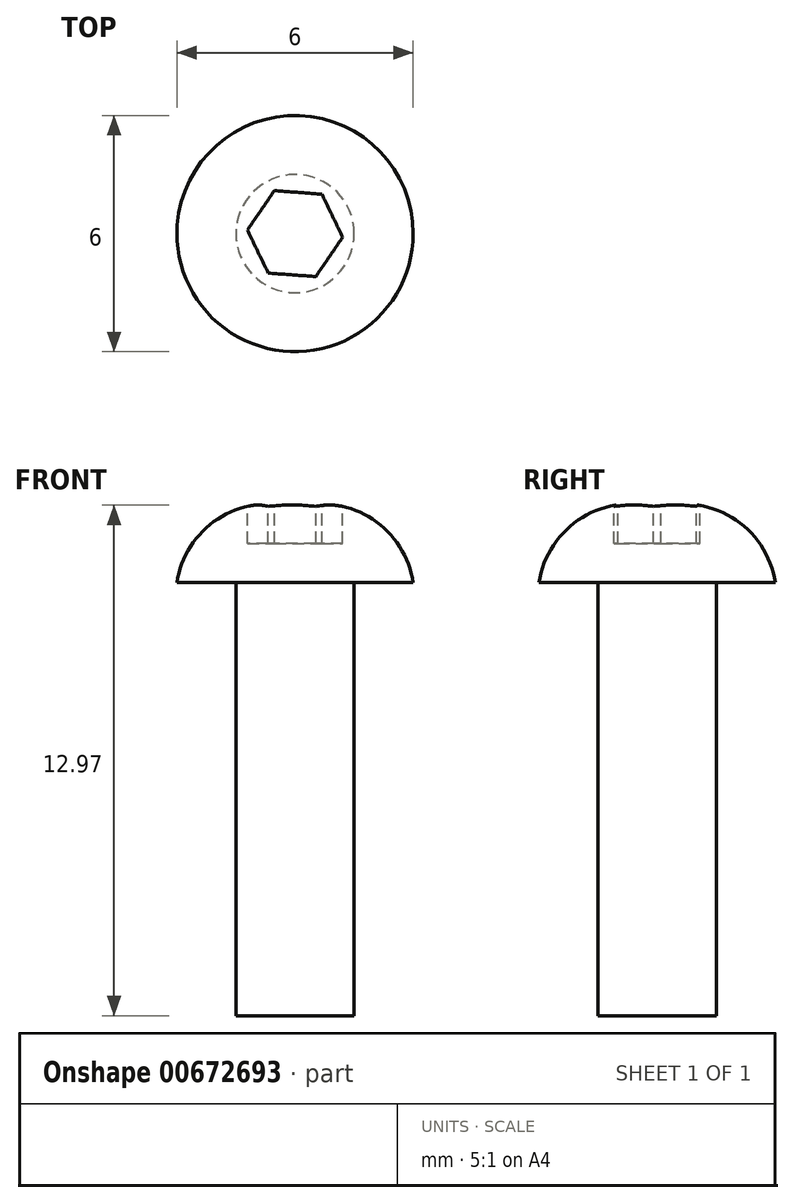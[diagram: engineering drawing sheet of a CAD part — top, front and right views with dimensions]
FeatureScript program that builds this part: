
annotation { "Feature Type Name" : "Feature", "Feature Type Description" : "" }
export const myFeature = defineFeature(function(context is Context, id is Id, definition is map)
    precondition{}
    {
        {
            var Q0;
            Q0=qCreatedBy(makeId("Top.planeOp"),FACE);
            var sketch = newSketch(context, id + "F0", { "sketchPlane" : qUnion([Q0])});
            skCircle(sketch, "E0", {"center": v(0, 0) * mm, "radius": 3 * mm});
            skCircle(sketch, "E1", {"center": v(0, 0) * mm, "radius": 1.5 * mm});
            skSolve(sketch);
        }
        {
            var Q0;
            Q0=makeQuery(id+"F0.imprint","IMPRINT",FACE,{"disambiguationData":[TD([[makeQuery(id+"F0.imprint","IMPRINT",EDGE,{"derivedFrom":sQuery(id+"F0.wireOp",EDGE,"E0")}),1.0]])]});
            var Q1;
            Q1=makeQuery(id+"F0.imprint","IMPRINT",FACE,{"disambiguationData":[TD([[makeQuery(id+"F0.imprint","IMPRINT",EDGE,{"derivedFrom":sQuery(id+"F0.wireOp",EDGE,"E1")}),1.0]])]});
            extrude(context, id + "F1", {"entities" : qUnion([Q0, Q1]), "depth" : 2 * mm, "offsetDistance" : 25 * mm});
        }
        {
            var Q0;
            Q0=makeQuery(id+"F0.imprint","IMPRINT",FACE,{"disambiguationData":[TD([[makeQuery(id+"F0.imprint","IMPRINT",EDGE,{"derivedFrom":sQuery(id+"F0.wireOp",EDGE,"E1")}),1.0]])]});
            extrude(context, id + "F2", {"entities" : qUnion([Q0]), "operationType" : NewBodyOperationType.ADD, "oppositeDirection" : true, "depth" : 11 * mm, "offsetDistance" : 25 * mm});
        }
        {
            var Q0;
            Q0=makeQuery(id+"F1.opExtrude","CAP_EDGE",EDGE,{"disambiguationData":[OSD([sQuery(id+"F0.wireOp",EDGE,"E0")])],"isStart":false});
            fillet(context, id + "F3", {"entities" : qUnion([Q0]), "radius" : 2.34 * mm, "tangentPropagation" : true, "allowEdgeOverflow" : false});
        }
        {
            var Q0;
            Q0=qCreatedBy(makeId("Top.planeOp"),FACE);
            cPlane(context, id + "F4", {"entities" : qUnion([Q0]), "cplaneType" : CPlaneType.OFFSET, "offset" : 2.5 * mm, "width" : 150 * mm, "height" : 150 * mm});
        }
        {
            var Q0;
            Q0=qCreatedBy(id+"F4.planeOp",FACE);
            var sketch = newSketch(context, id + "F5", { "sketchPlane" : qUnion([Q0])});
            skCircle(sketch, "E2.cCircle", {"center": v(0, 0) * mm, "radius": 1.05 * mm, "construction": true});
            skLineSegment(sketch, "E2.0", {"start": v(1.2, -0.09) * mm, "end": v(0.53, -1.1) * mm});
            skLineSegment(sketch, "E2.1", {"start": v(0.53, -1.1) * mm, "end": v(-0.68, -1) * mm});
            skLineSegment(sketch, "E2.2", {"start": v(-0.68, -1) * mm, "end": v(-1.2, 0.09) * mm});
            skLineSegment(sketch, "E2.3", {"start": v(-1.2, 0.09) * mm, "end": v(-0.53, 1.1) * mm});
            skLineSegment(sketch, "E2.4", {"start": v(-0.53, 1.1) * mm, "end": v(0.68, 1) * mm});
            skLineSegment(sketch, "E2.5", {"start": v(0.68, 1) * mm, "end": v(1.2, -0.09) * mm});
            skPoint(sketch, "E2.0.midPoint", {"position": v(0.87, -0.6) * mm});
            skSolve(sketch);
        }
        {
            var Q0;
            Q0=makeQuery(id+"F5.imprint","IMPRINT",FACE,{"disambiguationData":[TD([[makeQuery(id+"F5.imprint","IMPRINT",EDGE,{"derivedFrom":sQuery(id+"F5.wireOp",EDGE,"E2.0")}),-1.0]])]});
            extrude(context, id + "F6", {"entities" : qUnion([Q0]), "operationType" : NewBodyOperationType.REMOVE, "oppositeDirection" : true, "depth" : 1.5 * mm, "offsetDistance" : 25 * mm});
        }
    });
